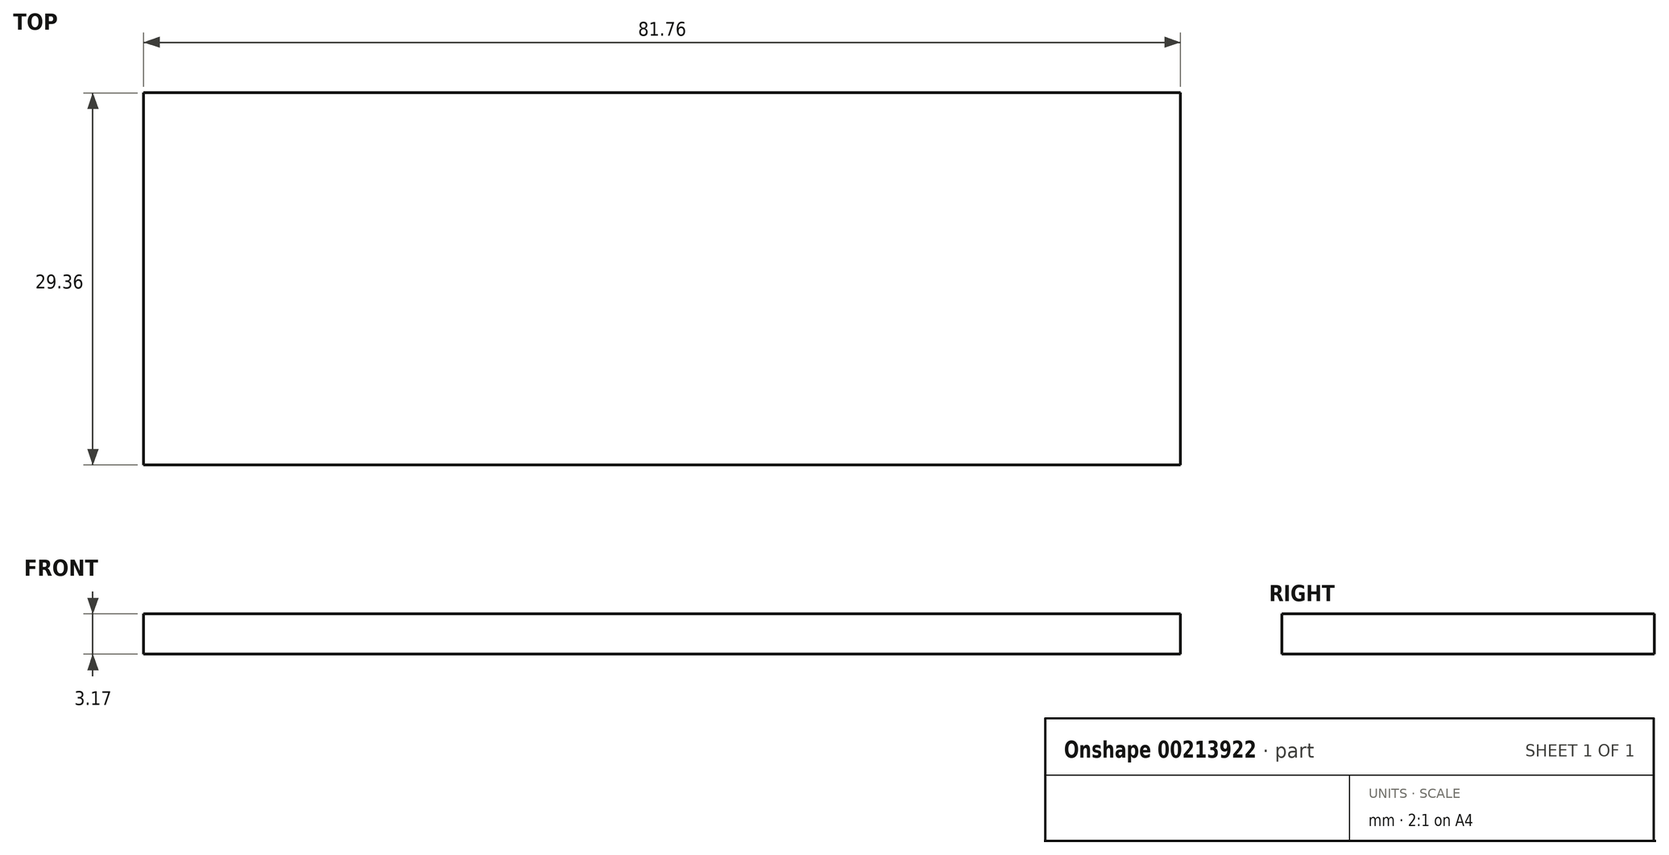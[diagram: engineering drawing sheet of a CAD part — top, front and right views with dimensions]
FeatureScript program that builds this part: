
annotation { "Feature Type Name" : "Feature", "Feature Type Description" : "" }
export const myFeature = defineFeature(function(context is Context, id is Id, definition is map)
    precondition{}
    {
        {
            var Q0;
            Q0=qCreatedBy(makeId("Top.planeOp"),FACE);
            var sketch = newSketch(context, id + "F0", { "sketchPlane" : qUnion([Q0])});
            skLineSegment(sketch, "E0.bottom", {"start": v(40.88, 14.68) * mm, "end": v(-40.88, 14.68) * mm});
            skLineSegment(sketch, "E0.top", {"start": v(40.88, -14.68) * mm, "end": v(-40.88, -14.68) * mm});
            skLineSegment(sketch, "E0.left", {"start": v(40.88, 14.68) * mm, "end": v(40.88, -14.68) * mm});
            skLineSegment(sketch, "E0.right", {"start": v(-40.88, 14.68) * mm, "end": v(-40.88, -14.68) * mm});
            skPoint(sketch, "E0.middle", {"position": v(0, 0) * mm});
            skSolve(sketch);
        }
        {
            var Q0;
            Q0=makeQuery(id+"F0.imprint","IMPRINT",FACE,{"disambiguationData":[TD([[makeQuery(id+"F0.imprint","IMPRINT",EDGE,{"derivedFrom":sQuery(id+"F0.wireOp",EDGE,"E0.bottom")}),1.0]])]});
            extrude(context, id + "F1", {"entities" : qUnion([Q0]), "depth" : 3.17 * mm});
        }
    });
